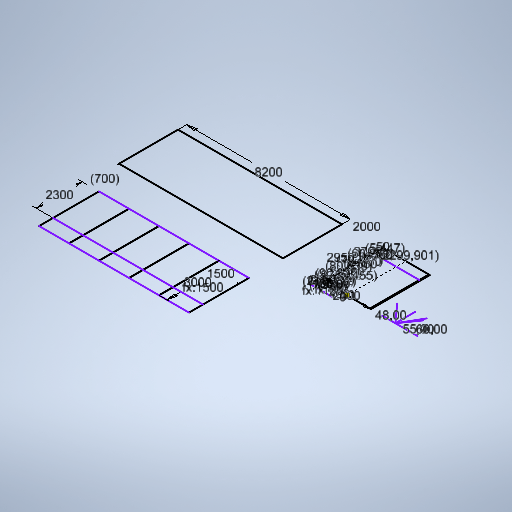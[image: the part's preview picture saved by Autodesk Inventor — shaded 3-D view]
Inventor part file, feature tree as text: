
AUTODESK INVENTOR PART (.ipt)
format: ipt  version: 2025 (Build 290162010, 162A)  size: 332,800 bytes
history: native  units: mm
features: sketch x2
ambient origin geometry x8: Origin, YZ Plane, XZ Plane, XY Plane, X Axis, Y Axis, Z Axis, Center Point
feature tree (2):
  sketch  "Sketch1"  dims[d0=2400.0mm]
  sketch  "Sketch Rectangular Pattern2"  dims[d1=2950.0mm d9=50.0mm d10=100.0mm d11=50.0mm d13=135.0deg d14=950.0mm d15=200.0mm d16=1150.0mm d17=200.0mm d18=23.743743mm d20=50.0mm d21=100.0mm d22=212.132034mm d23=8200.0mm d24=2000.0mm d27=1500.0mm d28=3000.0mm d36=50.0mm d38=1500.0mm d39=10.0mm d41=10.0mm d43=2750.454508mm d44=55.0mm d45=400.0mm d46=400.0mm d47=0.0mm d48=300.0mm d50=560.0mm d51=560.0mm d52=560.0mm d53=560.0mm d54=5.44707mm d55=2300.0mm d56=2299.900979mm d66=700.0mm d68=200.0mm d69=90.834574mm d70=80.639428mm d71=70.470938mm d73=60.28912mm d74=60.0deg d75=9.599311mm d76=8.37758mm d77=2705.0mm d78=460.0mm]
